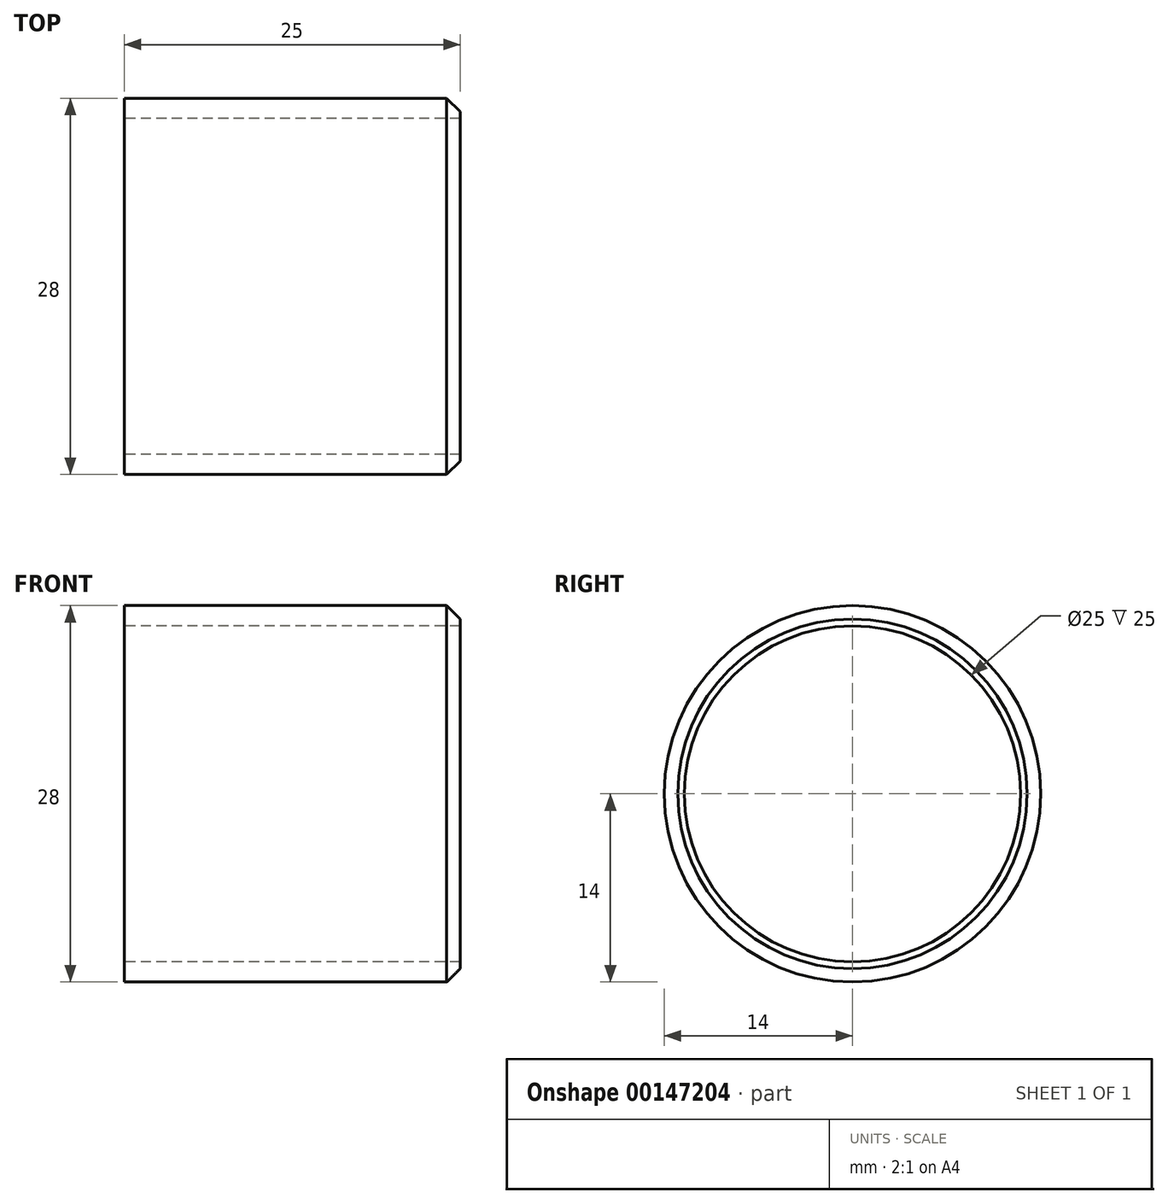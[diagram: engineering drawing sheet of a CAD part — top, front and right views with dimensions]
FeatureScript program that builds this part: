
annotation { "Feature Type Name" : "Feature", "Feature Type Description" : "" }
export const myFeature = defineFeature(function(context is Context, id is Id, definition is map)
    precondition{}
    {
        {
            var Q0;
            Q0=qCreatedBy(makeId("Right.planeOp"),FACE);
            var sketch = newSketch(context, id + "F0", { "sketchPlane" : qUnion([Q0])});
            skCircle(sketch, "E0", {"center": v(0, 0) * mm, "radius": 14 * mm});
            skCircle(sketch, "E1", {"center": v(0, 0) * mm, "radius": 12.5 * mm});
            skSolve(sketch);
        }
        {
            var Q0;
            Q0 = qSketchRegion(id + "F0", true);
            extrude(context, id + "F1", {"entities" : qUnion([Q0]), "depth" : 25 * mm});
        }
        {
            var Q0;
            Q0=makeQuery(id+"F1.opExtrude","CAP_EDGE",EDGE,{"disambiguationData":[OSD([sQuery(id+"F0.wireOp",EDGE,"E0")])],"isStart":false});
            chamfer(context, id + "F2", {"entities" : qUnion([Q0]), "width" : 1 * mm, "tangentPropagation" : true});
        }
    });
